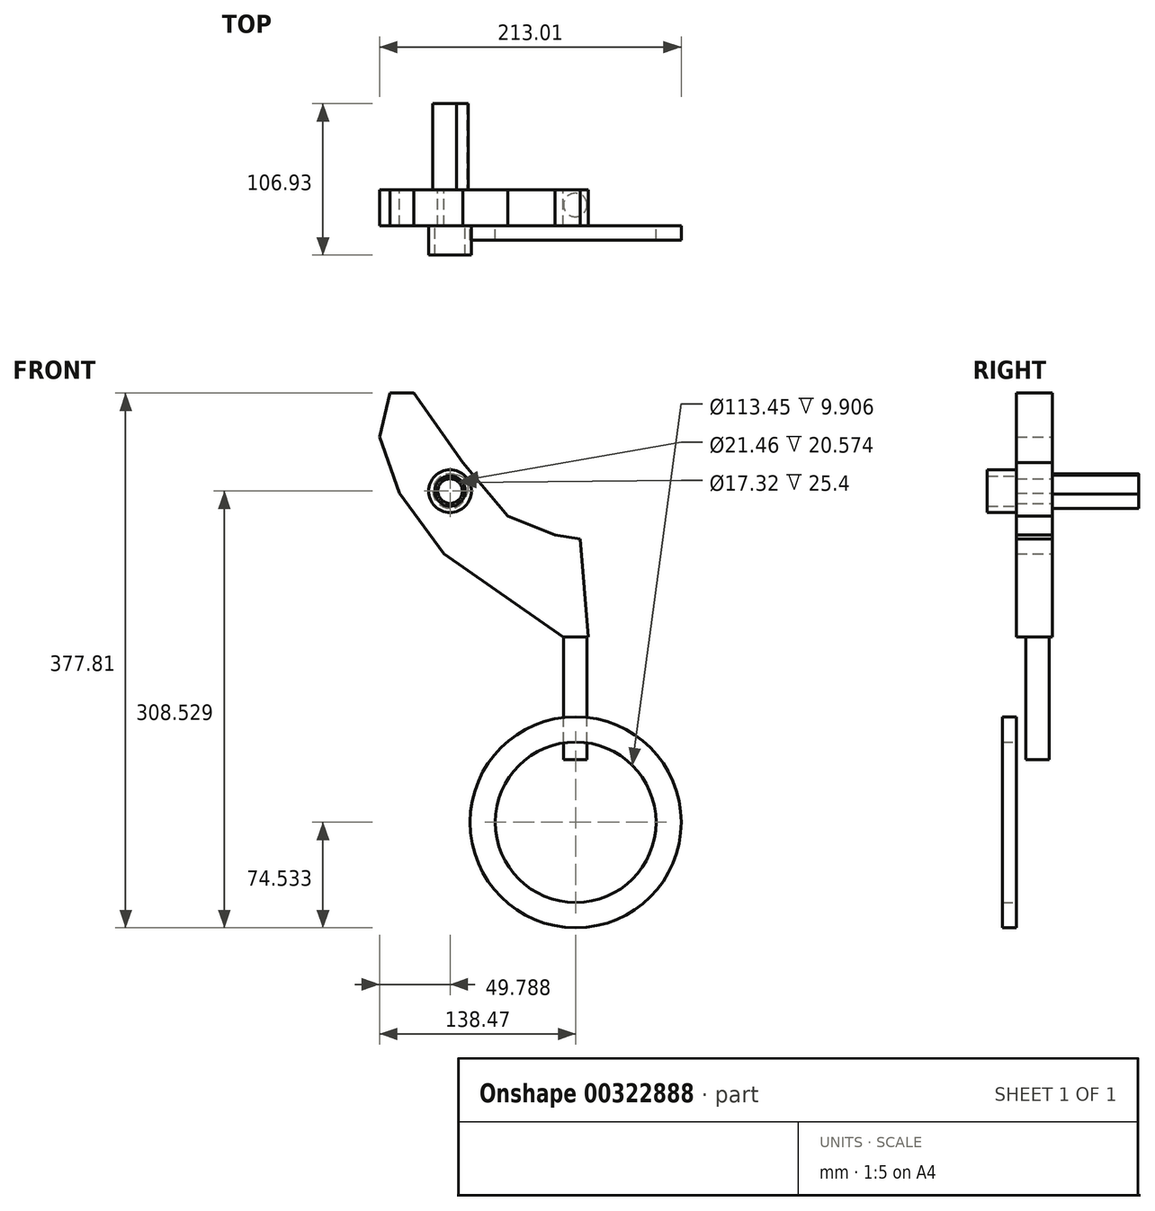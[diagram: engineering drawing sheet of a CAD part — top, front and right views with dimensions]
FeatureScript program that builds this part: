
annotation { "Feature Type Name" : "Feature", "Feature Type Description" : "" }
export const myFeature = defineFeature(function(context is Context, id is Id, definition is map)
    precondition{}
    {
        {
            var Q0;
            Q0=qCreatedBy(makeId("Front.planeOp"),FACE);
            var sketch = newSketch(context, id + "F0", { "sketchPlane" : qUnion([Q0])});
            skLineSegment(sketch, "E0", {"start": v(46.82, 30.2) * mm, "end": v(52.48, -41.92) * mm});
            skLineSegment(sketch, "E1", {"start": v(52.48, -41.92) * mm, "end": v(70.35, -41.92) * mm});
            skLineSegment(sketch, "E2", {"start": v(70.35, -41.92) * mm, "end": v(64.54, 27.3) * mm});
            skLineSegment(sketch, "E3", {"start": v(64.54, 27.3) * mm, "end": v(46.82, 30.2) * mm});
            skLineSegment(sketch, "E4", {"start": v(46.82, 30.2) * mm, "end": v(13.3, 43.33) * mm});
            skLineSegment(sketch, "E5", {"start": v(13.3, 43.33) * mm, "end": v(-18.35, 81.17) * mm});
            skLineSegment(sketch, "E6", {"start": v(-18.35, 81.17) * mm, "end": v(-52.78, 130.35) * mm});
            skLineSegment(sketch, "E7", {"start": v(-52.78, 130.35) * mm, "end": v(-69.67, 130.35) * mm});
            skLineSegment(sketch, "E8", {"start": v(-69.67, 130.35) * mm, "end": v(-77.16, 99.45) * mm});
            skLineSegment(sketch, "E9", {"start": v(-77.16, 99.45) * mm, "end": v(-63.22, 59.62) * mm});
            skLineSegment(sketch, "E10", {"start": v(-63.22, 59.62) * mm, "end": v(-31.57, 16.9) * mm});
            skLineSegment(sketch, "E11", {"start": v(-31.57, 16.9) * mm, "end": v(52.48, -41.92) * mm});
            skCircle(sketch, "E12", {"center": v(-27.37, 61.07) * mm, "radius": 8.66 * mm});
            skCircle(sketch, "E13", {"center": v(-27.37, 61.07) * mm, "radius": 6.5 * mm});
            skSolve(sketch);
        }
        {
            var Q0;
            Q0 = qSketchRegion(id + "F0", true);
            extrude(context, id + "F1", {"entities" : qUnion([Q0]), "depth" : 25.4 * mm});
        }
        {
            var Q0;
            Q0=makeQuery(id+"F1.opExtrude","CAP_FACE",FACE,{"disambiguationData":[OSD([sQuery(id+"F0.wireOp",EDGE,"E1"),sQuery(id+"F0.wireOp",EDGE,"E2"),sQuery(id+"F0.wireOp",EDGE,"E3"),sQuery(id+"F0.wireOp",EDGE,"E4"),sQuery(id+"F0.wireOp",EDGE,"E5"),sQuery(id+"F0.wireOp",EDGE,"E6"),sQuery(id+"F0.wireOp",EDGE,"E7"),sQuery(id+"F0.wireOp",EDGE,"E8"),sQuery(id+"F0.wireOp",EDGE,"E9"),sQuery(id+"F0.wireOp",EDGE,"E10"),sQuery(id+"F0.wireOp",EDGE,"E11"),sQuery(id+"F0.wireOp",EDGE,"E12")])],"isStart":true});
            var sketch = newSketch(context, id + "F2", { "sketchPlane" : qUnion([Q0])});
            skCircle(sketch, "E14", {"center": v(27.37, 61.07) * mm, "radius": 12.11 * mm});
            skCircle(sketch, "E15", {"center": v(23.61, 63.18) * mm, "radius": 9.19 * mm});
            skSolve(sketch);
        }
        {
            var Q0;
            Q0 = qSketchRegion(id + "F2", true);
            extrude(context, id + "F3", {"entities" : qUnion([Q0]), "operationType" : NewBodyOperationType.ADD, "depth" : 60.96 * mm});
        }
        {
            var Q0;
            Q0=makeQuery(id+"F1.opExtrude","CAP_FACE",FACE,{"disambiguationData":[OSD([sQuery(id+"F0.wireOp",EDGE,"E1"),sQuery(id+"F0.wireOp",EDGE,"E2"),sQuery(id+"F0.wireOp",EDGE,"E3"),sQuery(id+"F0.wireOp",EDGE,"E4"),sQuery(id+"F0.wireOp",EDGE,"E5"),sQuery(id+"F0.wireOp",EDGE,"E6"),sQuery(id+"F0.wireOp",EDGE,"E7"),sQuery(id+"F0.wireOp",EDGE,"E8"),sQuery(id+"F0.wireOp",EDGE,"E9"),sQuery(id+"F0.wireOp",EDGE,"E10"),sQuery(id+"F0.wireOp",EDGE,"E11"),sQuery(id+"F0.wireOp",EDGE,"E12")])],"isStart":false});
            var sketch = newSketch(context, id + "F4", { "sketchPlane" : qUnion([Q0])});
            skCircle(sketch, "E16", {"center": v(-27.37, 61.07) * mm, "radius": 10.73 * mm});
            skCircle(sketch, "E17", {"center": v(-27.37, 61.07) * mm, "radius": 15.04 * mm});
            skSolve(sketch);
        }
        {
            var Q0;
            Q0 = qSketchRegion(id + "F4", true);
            extrude(context, id + "F5", {"entities" : qUnion([Q0]), "operationType" : NewBodyOperationType.ADD, "depth" : 20.57 * mm});
        }
        {
            var Q0;
            Q0=makeQuery(id+"F1.opExtrude","SWEPT_FACE",FACE,{"disambiguationData":[OSD([sQuery(id+"F0.wireOp",EDGE,"E1")])]});
            var sketch = newSketch(context, id + "F6", { "sketchPlane" : qUnion([Q0])});
            skCircle(sketch, "E18", {"center": v(61.05, 10.56) * mm, "radius": 8.3 * mm});
            skSolve(sketch);
        }
        {
            var Q0;
            Q0 = qSketchRegion(id + "F6", true);
            extrude(context, id + "F7", {"entities" : qUnion([Q0]), "operationType" : NewBodyOperationType.ADD, "depth" : 86.61 * mm});
        }
        {
            var Q0;
            {var subQ0=sQuery(id+"F0.wireOp",EDGE,"E9");var subQ1=sQuery(id+"F0.wireOp",EDGE,"E8");var subQ2=sQuery(id+"F0.wireOp",EDGE,"E7");var subQ3=sQuery(id+"F0.wireOp",EDGE,"E6");var subQ4=sQuery(id+"F0.wireOp",EDGE,"E5");var subQ5=sQuery(id+"F0.wireOp",EDGE,"E10");var subQ6=sQuery(id+"F0.wireOp",EDGE,"E1");var subQ7=sQuery(id+"F0.wireOp",EDGE,"E4");var subQ8=sQuery(id+"F0.wireOp",EDGE,"E2");var subQ9=sQuery(id+"F0.wireOp",EDGE,"E3");var subQ10=sQuery(id+"F0.wireOp",EDGE,"E11");Q0=makeQuery(id+"F5.boolean.opBoolean","SPLIT",FACE,{"disambiguationData":[TD([makeQuery(id+"F1.opExtrude","SWEPT_FACE",FACE,{"disambiguationData":[OSD([subQ6])]})])],"derivedFrom":makeQuery(id+"F1.opExtrude","CAP_FACE",FACE,{"disambiguationData":[OSD([subQ6,subQ8,subQ9,subQ7,subQ4,subQ3,subQ2,subQ1,subQ0,subQ5,subQ10,sQuery(id+"F0.wireOp",EDGE,"E12")])],"isStart":false})});}
            var sketch = newSketch(context, id + "F8", { "sketchPlane" : qUnion([Q0])});
            skCircle(sketch, "E19", {"center": v(61.31, -172.93) * mm, "radius": 56.72 * mm});
            skCircle(sketch, "E20", {"center": v(61.31, -172.93) * mm, "radius": 74.54 * mm});
            skSolve(sketch);
        }
        {
            var Q0;
            Q0 = qSketchRegion(id + "F8", true);
            extrude(context, id + "F9", {"entities" : qUnion([Q0]), "depth" : 9.9 * mm});
        }
    });
